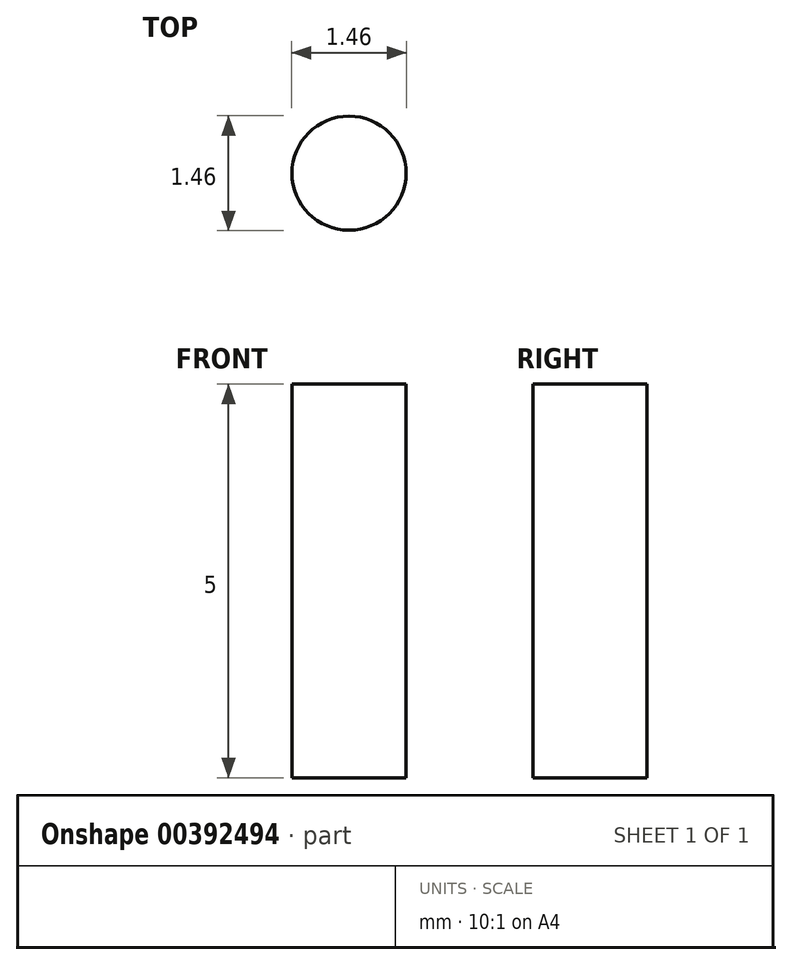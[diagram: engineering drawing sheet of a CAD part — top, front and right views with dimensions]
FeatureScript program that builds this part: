
annotation { "Feature Type Name" : "Feature", "Feature Type Description" : "" }
export const myFeature = defineFeature(function(context is Context, id is Id, definition is map)
    precondition{}
    {
        {
            var Q0;
            Q0=qCreatedBy(makeId("Top.planeOp"),FACE);
            var sketch = newSketch(context, id + "F0", { "sketchPlane" : qUnion([Q0])});
            skCircle(sketch, "E0", {"center": v(0, 0) * mm, "radius": 0.73 * mm});
            skSolve(sketch);
        }
        {
            var Q0;
            Q0 = qSketchRegion(id + "F0", true);
            extrude(context, id + "F1", {"entities" : qUnion([Q0]), "depth" : 5 * mm});
        }
    });
